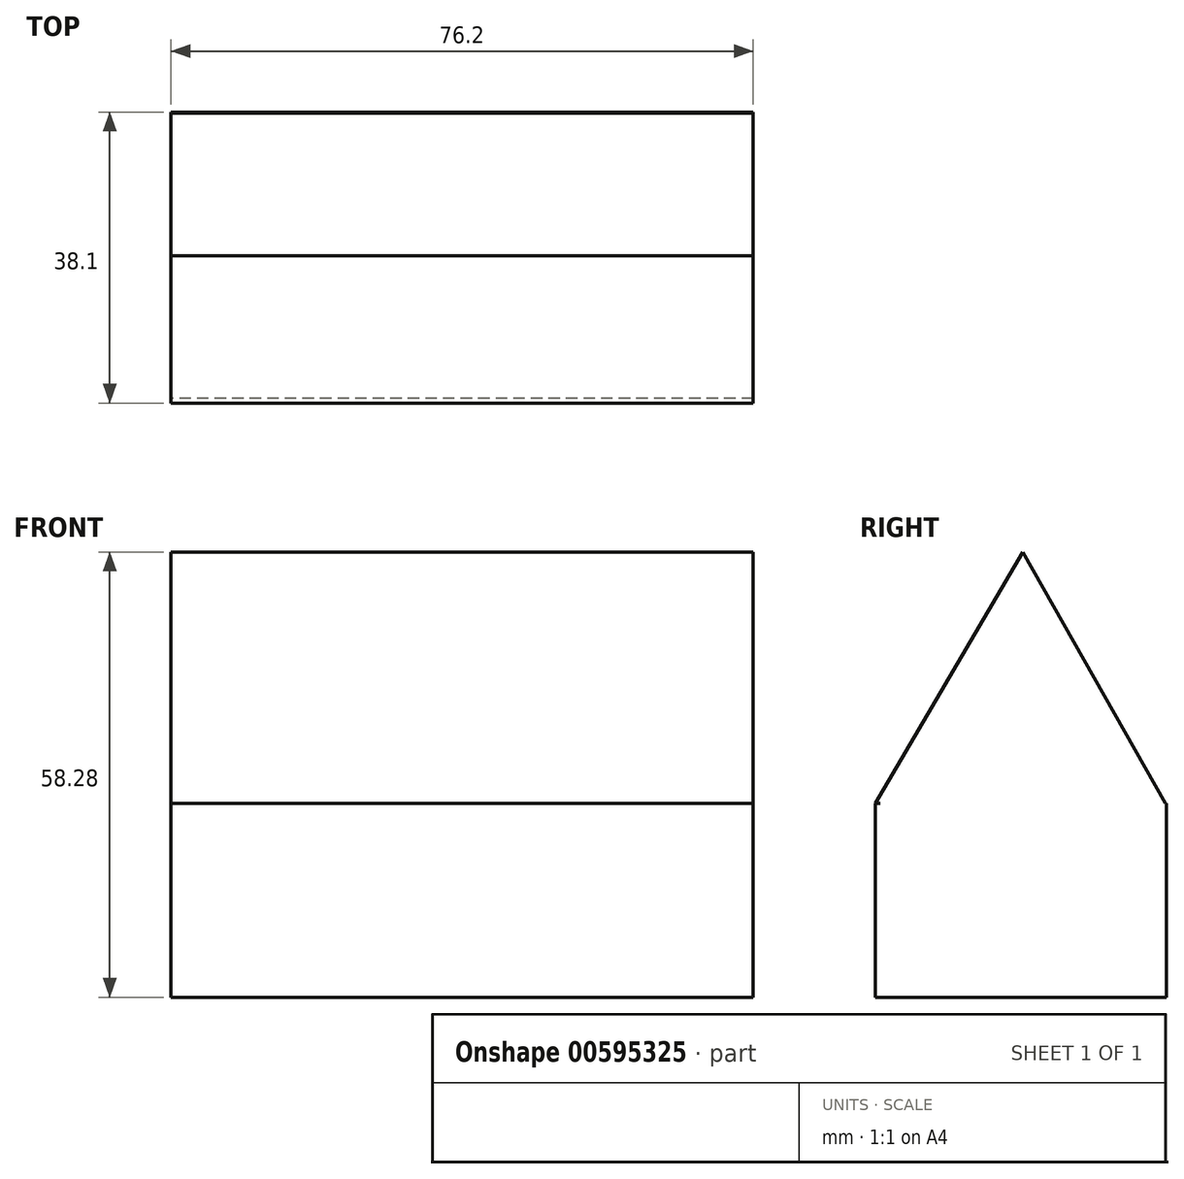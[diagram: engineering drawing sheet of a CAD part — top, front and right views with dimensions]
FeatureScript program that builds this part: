
annotation { "Feature Type Name" : "Feature", "Feature Type Description" : "" }
export const myFeature = defineFeature(function(context is Context, id is Id, definition is map)
    precondition{}
    {
        {
            var Q0;
            Q0=qCreatedBy(makeId("Top.planeOp"),FACE);
            var sketch = newSketch(context, id + "F0", { "sketchPlane" : qUnion([Q0])});
            skLineSegment(sketch, "E0.bottom", {"start": v(0, 0) * mm, "end": v(-76.2, 0) * mm});
            skLineSegment(sketch, "E0.top", {"start": v(0, 38.1) * mm, "end": v(-76.2, 38.1) * mm});
            skLineSegment(sketch, "E0.left", {"start": v(0, 0) * mm, "end": v(0, 38.1) * mm});
            skLineSegment(sketch, "E0.right", {"start": v(-76.2, 0) * mm, "end": v(-76.2, 38.1) * mm});
            skSolve(sketch);
        }
        {
            var Q0;
            Q0=makeQuery(id+"F0.imprint","IMPRINT",FACE,{"disambiguationData":[TD([[makeQuery(id+"F0.imprint","IMPRINT",EDGE,{"derivedFrom":sQuery(id+"F0.wireOp",EDGE,"E0.bottom")}),-1.0]])]});
            extrude(context, id + "F1", {"entities" : qUnion([Q0]), "depth" : 25.4 * mm, "offsetDistance" : 25.4 * mm});
        }
        {
            var Q0;
            Q0=qCreatedBy(makeId("Right.planeOp"),FACE);
            var sketch = newSketch(context, id + "F2", { "sketchPlane" : qUnion([Q0])});
            skCircle(sketch, "E1.cCircle", {"center": v(19.12, 36.28) * mm, "radius": 11 * mm, "construction": true});
            skLineSegment(sketch, "E1.0", {"start": v(19.26, 58.28) * mm, "end": v(38.1, 25.16) * mm});
            skLineSegment(sketch, "E1.1", {"start": v(38.1, 25.16) * mm, "end": v(0, 25.4) * mm});
            skLineSegment(sketch, "E1.2", {"start": v(0, 25.4) * mm, "end": v(19.26, 58.28) * mm});
            skPoint(sketch, "E1.0.midPoint", {"position": v(28.68, 41.72) * mm});
            skSolve(sketch);
        }
        {
            var Q0;
            Q0=makeQuery(id+"F2.imprint","IMPRINT",FACE,{"disambiguationData":[TD([[makeQuery(id+"F2.imprint","IMPRINT",EDGE,{"derivedFrom":sQuery(id+"F2.wireOp",EDGE,"E1.0")}),-1.0]])]});
            extrude(context, id + "F3", {"entities" : qUnion([Q0]), "operationType" : NewBodyOperationType.ADD, "depth" : -76.2 * mm, "offsetDistance" : 25.4 * mm});
        }
    });
